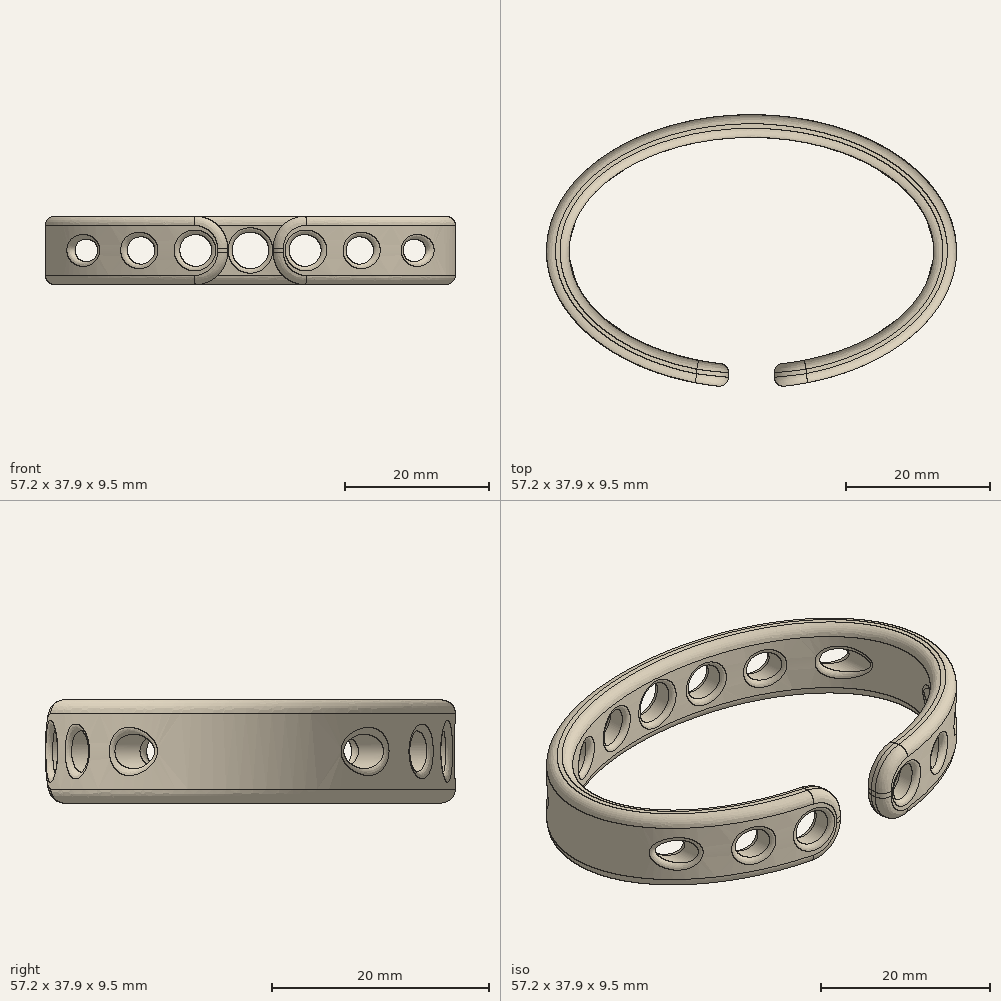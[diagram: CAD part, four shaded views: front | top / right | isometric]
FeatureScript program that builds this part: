
annotation { "Feature Type Name" : "Feature", "Feature Type Description" : "" }
export const myFeature = defineFeature(function(context is Context, id is Id, definition is map)
    precondition{}
    {
        {
            var Q0;
            Q0=qCreatedBy(makeId("Top.planeOp"),FACE);
            var sketch = newSketch(context, id + "F0", { "sketchPlane" : qUnion([Q0])});
            skEllipticalArc(sketch, "E0", {});
            skEllipticalArc(sketch, "E1", {});
            skLineSegment(sketch, "E2.left", {"start": v(-3.18, -17.54) * mm, "end": v(-3.18, -16.9) * mm});
            skLineSegment(sketch, "E2.right", {"start": v(3.17, -17.54) * mm, "end": v(3.17, -16.9) * mm});
            skPoint(sketch, "E3.end.orphan", {"position": v(0, -19.05) * mm});
            skPoint(sketch, "E4.visualSharp", {"position": v(-3.18, -18.93) * mm});
            skArc(sketch, "E4.filletArc", {"start": v(-4.58, -18.8) * mm, "mid": v(-3.6, -18.49) * mm, "end": v(-3.18, -17.54) * mm});
            skPoint(sketch, "E5.visualSharp", {"position": v(3.18, -18.93) * mm});
            skArc(sketch, "E5.filletArc", {"start": v(3.17, -17.54) * mm, "mid": v(3.6, -18.49) * mm, "end": v(4.58, -18.8) * mm});
            skPoint(sketch, "E6.visualSharp", {"position": v(3.17, -15.75) * mm});
            skArc(sketch, "E6.filletArc", {"start": v(4.3, -15.64) * mm, "mid": v(3.5, -16.06) * mm, "end": v(3.17, -16.9) * mm});
            skPoint(sketch, "E7.visualSharp", {"position": v(-3.18, -15.75) * mm});
            skArc(sketch, "E7.filletArc", {"start": v(-3.18, -16.9) * mm, "mid": v(-3.5, -16.06) * mm, "end": v(-4.3, -15.64) * mm});
            const initialGuessF0  = {"E0": [0, 0, 1, 0, 0.0254, 0.015875, 4.8828647943944, 4.541913166455214], "E1": [0, 0, 1, 0, 0.028575, 0.01905, 4.873424775599793, 4.551353185169586]};
            skSetInitialGuess(sketch, initialGuessF0);
            skSolve(sketch);
        }
        {
            var Q0;
            Q0=makeQuery(id+"F0.imprint","IMPRINT",FACE,{"disambiguationData":[TD([[makeQuery(id+"F0.imprint","IMPRINT",EDGE,{"derivedFrom":sQuery(id+"F0.wireOp",EDGE,"E0")}),-1.0]])]});
            extrude(context, id + "F1", {"entities" : qUnion([Q0]), "depth" : 9.52 * mm});
        }
        {
            var Q0;
            Q0=makeQuery(id+"F1.opExtrude","CAP_EDGE",EDGE,{"disambiguationData":[OSD([sQuery(id+"F0.wireOp",EDGE,"E2.left")])],"isStart":false});
            var Q1;
            Q1=makeQuery(id+"F1.opExtrude","CAP_EDGE",EDGE,{"disambiguationData":[OSD([sQuery(id+"F0.wireOp",EDGE,"E2.left")])],"isStart":true});
            var Q2;
            Q2=makeQuery(id+"F1.opExtrude","CAP_EDGE",EDGE,{"disambiguationData":[OSD([sQuery(id+"F0.wireOp",EDGE,"E2.right")])],"isStart":false});
            var Q3;
            Q3=makeQuery(id+"F1.opExtrude","CAP_EDGE",EDGE,{"disambiguationData":[OSD([sQuery(id+"F0.wireOp",EDGE,"E2.right")])],"isStart":true});
            fillet(context, id + "F2", {"entities" : qUnion([Q0, Q1, Q2, Q3]), "radius" : 4.44 * mm, "allowEdgeOverflow" : false});
        }
        {
            var Q0;
            Q0=makeQuery(id+"F1.opExtrude","CAP_EDGE",EDGE,{"disambiguationData":[OSD([sQuery(id+"F0.wireOp",EDGE,"E1")])],"isStart":false});
            var Q1;
            Q1=makeQuery(id+"F1.opExtrude","CAP_EDGE",EDGE,{"disambiguationData":[OSD([sQuery(id+"F0.wireOp",EDGE,"E0")])],"isStart":false});
            var Q2;
            Q2=makeQuery(id+"F1.opExtrude","CAP_EDGE",EDGE,{"disambiguationData":[OSD([sQuery(id+"F0.wireOp",EDGE,"E1")])],"isStart":true});
            var Q3;
            Q3=makeQuery(id+"F1.opExtrude","CAP_EDGE",EDGE,{"disambiguationData":[OSD([sQuery(id+"F0.wireOp",EDGE,"E0")])],"isStart":true});
            fillet(context, id + "F3", {"entities" : qUnion([Q0, Q1, Q2, Q3]), "radius" : 1.27 * mm, "tangentPropagation" : true, "allowEdgeOverflow" : false});
        }
        {
            var Q0;
            Q0=qCreatedBy(makeId("Front.planeOp"),FACE);
            var sketch = newSketch(context, id + "F4", { "sketchPlane" : qUnion([Q0])});
            skCircle(sketch, "E8", {"center": v(-7.62, 4.76) * mm, "radius": 2.22 * mm});
            skCircle(sketch, "E9", {"center": v(0, 4.76) * mm, "radius": 2.54 * mm});
            skCircle(sketch, "E10", {"center": v(7.62, 4.76) * mm, "radius": 2.22 * mm});
            skCircle(sketch, "E11", {"center": v(-15.24, 4.76) * mm, "radius": 1.9 * mm});
            skCircle(sketch, "E12", {"center": v(15.24, 4.76) * mm, "radius": 1.9 * mm});
            skCircle(sketch, "E13", {"center": v(-22.86, 4.76) * mm, "radius": 1.59 * mm});
            skCircle(sketch, "E14", {"center": v(22.86, 4.76) * mm, "radius": 1.59 * mm});
            skSolve(sketch);
        }
        {
            var Q0;
            Q0=makeQuery(id+"F4.imprint","IMPRINT",FACE,{"disambiguationData":[TD([[makeQuery(id+"F4.imprint","IMPRINT",EDGE,{"derivedFrom":sQuery(id+"F4.wireOp",EDGE,"E13")}),1.0]])]});
            var Q1;
            Q1=makeQuery(id+"F4.imprint","IMPRINT",FACE,{"disambiguationData":[TD([[makeQuery(id+"F4.imprint","IMPRINT",EDGE,{"derivedFrom":sQuery(id+"F4.wireOp",EDGE,"E11")}),1.0]])]});
            var Q2;
            Q2=makeQuery(id+"F4.imprint","IMPRINT",FACE,{"disambiguationData":[TD([[makeQuery(id+"F4.imprint","IMPRINT",EDGE,{"derivedFrom":sQuery(id+"F4.wireOp",EDGE,"E8")}),1.0]])]});
            var Q3;
            Q3=makeQuery(id+"F4.imprint","IMPRINT",FACE,{"disambiguationData":[TD([[makeQuery(id+"F4.imprint","IMPRINT",EDGE,{"derivedFrom":sQuery(id+"F4.wireOp",EDGE,"E9")}),1.0]])]});
            var Q4;
            Q4=makeQuery(id+"F4.imprint","IMPRINT",FACE,{"disambiguationData":[TD([[makeQuery(id+"F4.imprint","IMPRINT",EDGE,{"derivedFrom":sQuery(id+"F4.wireOp",EDGE,"E10")}),1.0]])]});
            var Q5;
            Q5=makeQuery(id+"F4.imprint","IMPRINT",FACE,{"disambiguationData":[TD([[makeQuery(id+"F4.imprint","IMPRINT",EDGE,{"derivedFrom":sQuery(id+"F4.wireOp",EDGE,"E12")}),1.0]])]});
            var Q6;
            Q6=makeQuery(id+"F4.imprint","IMPRINT",FACE,{"disambiguationData":[TD([[makeQuery(id+"F4.imprint","IMPRINT",EDGE,{"derivedFrom":sQuery(id+"F4.wireOp",EDGE,"E14")}),1.0]])]});
            extrude(context, id + "F5", {"entities" : qUnion([Q0, Q1, Q2, Q3, Q4, Q5, Q6]), "operationType" : NewBodyOperationType.REMOVE, "endBound" : BoundingType.SYMMETRIC, "depth" : 50.8 * mm});
        }
        {
            var Q0;
            Q0=makeQuery(id+"F5.boolean.opBoolean","INTERSECT",EDGE,{"disambiguationData":[OD(1.0)],"derivedFrom":[makeQuery(id+"F1.opExtrude","SWEPT_FACE",FACE,{"disambiguationData":[OSD([sQuery(id+"F0.wireOp",EDGE,"E0")])]}),makeQuery(id+"F5.opExtrude","SWEPT_FACE",FACE,{"disambiguationData":[OSD([sQuery(id+"F4.wireOp",EDGE,"E13")])]})]});
            var Q1;
            Q1=makeQuery(id+"F5.boolean.opBoolean","INTERSECT",EDGE,{"disambiguationData":[OD(1.0)],"derivedFrom":[makeQuery(id+"F1.opExtrude","SWEPT_FACE",FACE,{"disambiguationData":[OSD([sQuery(id+"F0.wireOp",EDGE,"E0")])]}),makeQuery(id+"F5.opExtrude","SWEPT_FACE",FACE,{"disambiguationData":[OSD([sQuery(id+"F4.wireOp",EDGE,"E11")])]})]});
            var Q2;
            Q2=makeQuery(id+"F5.boolean.opBoolean","INTERSECT",EDGE,{"disambiguationData":[OD(1.0)],"derivedFrom":[makeQuery(id+"F1.opExtrude","SWEPT_FACE",FACE,{"disambiguationData":[OSD([sQuery(id+"F0.wireOp",EDGE,"E0")])]}),makeQuery(id+"F5.opExtrude","SWEPT_FACE",FACE,{"disambiguationData":[OSD([sQuery(id+"F4.wireOp",EDGE,"E8")])]})]});
            var Q3;
            Q3=makeQuery(id+"F5.boolean.opBoolean","INTERSECT",EDGE,{"derivedFrom":[makeQuery(id+"F1.opExtrude","SWEPT_FACE",FACE,{"disambiguationData":[OSD([sQuery(id+"F0.wireOp",EDGE,"E0")])]}),makeQuery(id+"F5.opExtrude","SWEPT_FACE",FACE,{"disambiguationData":[OSD([sQuery(id+"F4.wireOp",EDGE,"E9")])]})]});
            var Q4;
            Q4=makeQuery(id+"F5.boolean.opBoolean","INTERSECT",EDGE,{"disambiguationData":[OD(1.0)],"derivedFrom":[makeQuery(id+"F1.opExtrude","SWEPT_FACE",FACE,{"disambiguationData":[OSD([sQuery(id+"F0.wireOp",EDGE,"E0")])]}),makeQuery(id+"F5.opExtrude","SWEPT_FACE",FACE,{"disambiguationData":[OSD([sQuery(id+"F4.wireOp",EDGE,"E10")])]})]});
            var Q5;
            Q5=makeQuery(id+"F5.boolean.opBoolean","INTERSECT",EDGE,{"disambiguationData":[OD(1.0)],"derivedFrom":[makeQuery(id+"F1.opExtrude","SWEPT_FACE",FACE,{"disambiguationData":[OSD([sQuery(id+"F0.wireOp",EDGE,"E0")])]}),makeQuery(id+"F5.opExtrude","SWEPT_FACE",FACE,{"disambiguationData":[OSD([sQuery(id+"F4.wireOp",EDGE,"E12")])]})]});
            var Q6;
            Q6=makeQuery(id+"F5.boolean.opBoolean","INTERSECT",EDGE,{"disambiguationData":[OD(1.0)],"derivedFrom":[makeQuery(id+"F1.opExtrude","SWEPT_FACE",FACE,{"disambiguationData":[OSD([sQuery(id+"F0.wireOp",EDGE,"E0")])]}),makeQuery(id+"F5.opExtrude","SWEPT_FACE",FACE,{"disambiguationData":[OSD([sQuery(id+"F4.wireOp",EDGE,"E14")])]})]});
            var Q7;
            Q7=makeQuery(id+"F5.boolean.opBoolean","INTERSECT",EDGE,{"disambiguationData":[OD(1.0)],"derivedFrom":[makeQuery(id+"F1.opExtrude","SWEPT_FACE",FACE,{"disambiguationData":[OSD([sQuery(id+"F0.wireOp",EDGE,"E1")])]}),makeQuery(id+"F5.opExtrude","SWEPT_FACE",FACE,{"disambiguationData":[OSD([sQuery(id+"F4.wireOp",EDGE,"E14")])]})]});
            var Q8;
            Q8=makeQuery(id+"F5.boolean.opBoolean","INTERSECT",EDGE,{"disambiguationData":[OD(1.0)],"derivedFrom":[makeQuery(id+"F1.opExtrude","SWEPT_FACE",FACE,{"disambiguationData":[OSD([sQuery(id+"F0.wireOp",EDGE,"E1")])]}),makeQuery(id+"F5.opExtrude","SWEPT_FACE",FACE,{"disambiguationData":[OSD([sQuery(id+"F4.wireOp",EDGE,"E12")])]})]});
            var Q9;
            Q9=makeQuery(id+"F5.boolean.opBoolean","INTERSECT",EDGE,{"disambiguationData":[OD(1.0)],"derivedFrom":[makeQuery(id+"F1.opExtrude","SWEPT_FACE",FACE,{"disambiguationData":[OSD([sQuery(id+"F0.wireOp",EDGE,"E1")])]}),makeQuery(id+"F5.opExtrude","SWEPT_FACE",FACE,{"disambiguationData":[OSD([sQuery(id+"F4.wireOp",EDGE,"E10")])]})]});
            var Q10;
            Q10=makeQuery(id+"F5.boolean.opBoolean","INTERSECT",EDGE,{"derivedFrom":[makeQuery(id+"F1.opExtrude","SWEPT_FACE",FACE,{"disambiguationData":[OSD([sQuery(id+"F0.wireOp",EDGE,"E1")])]}),makeQuery(id+"F5.opExtrude","SWEPT_FACE",FACE,{"disambiguationData":[OSD([sQuery(id+"F4.wireOp",EDGE,"E9")])]})]});
            var Q11;
            Q11=makeQuery(id+"F5.boolean.opBoolean","INTERSECT",EDGE,{"disambiguationData":[OD(1.0)],"derivedFrom":[makeQuery(id+"F1.opExtrude","SWEPT_FACE",FACE,{"disambiguationData":[OSD([sQuery(id+"F0.wireOp",EDGE,"E1")])]}),makeQuery(id+"F5.opExtrude","SWEPT_FACE",FACE,{"disambiguationData":[OSD([sQuery(id+"F4.wireOp",EDGE,"E8")])]})]});
            var Q12;
            Q12=makeQuery(id+"F5.boolean.opBoolean","INTERSECT",EDGE,{"disambiguationData":[OD(1.0)],"derivedFrom":[makeQuery(id+"F1.opExtrude","SWEPT_FACE",FACE,{"disambiguationData":[OSD([sQuery(id+"F0.wireOp",EDGE,"E1")])]}),makeQuery(id+"F5.opExtrude","SWEPT_FACE",FACE,{"disambiguationData":[OSD([sQuery(id+"F4.wireOp",EDGE,"E11")])]})]});
            var Q13;
            Q13=makeQuery(id+"F5.boolean.opBoolean","INTERSECT",EDGE,{"disambiguationData":[OD(1.0)],"derivedFrom":[makeQuery(id+"F1.opExtrude","SWEPT_FACE",FACE,{"disambiguationData":[OSD([sQuery(id+"F0.wireOp",EDGE,"E1")])]}),makeQuery(id+"F5.opExtrude","SWEPT_FACE",FACE,{"disambiguationData":[OSD([sQuery(id+"F4.wireOp",EDGE,"E13")])]})]});
            var Q14;
            Q14=makeQuery(id+"F5.boolean.opBoolean","INTERSECT",EDGE,{"disambiguationData":[OD(0.0)],"derivedFrom":[makeQuery(id+"F1.opExtrude","SWEPT_FACE",FACE,{"disambiguationData":[OSD([sQuery(id+"F0.wireOp",EDGE,"E0")])]}),makeQuery(id+"F5.opExtrude","SWEPT_FACE",FACE,{"disambiguationData":[OSD([sQuery(id+"F4.wireOp",EDGE,"E8")])]})]});
            var Q15;
            Q15=makeQuery(id+"F5.boolean.opBoolean","INTERSECT",EDGE,{"disambiguationData":[OD(0.0)],"derivedFrom":[makeQuery(id+"F1.opExtrude","SWEPT_FACE",FACE,{"disambiguationData":[OSD([sQuery(id+"F0.wireOp",EDGE,"E1")])]}),makeQuery(id+"F5.opExtrude","SWEPT_FACE",FACE,{"disambiguationData":[OSD([sQuery(id+"F4.wireOp",EDGE,"E8")])]})]});
            var Q16;
            Q16=makeQuery(id+"F5.boolean.opBoolean","INTERSECT",EDGE,{"disambiguationData":[OD(0.0)],"derivedFrom":[makeQuery(id+"F1.opExtrude","SWEPT_FACE",FACE,{"disambiguationData":[OSD([sQuery(id+"F0.wireOp",EDGE,"E1")])]}),makeQuery(id+"F5.opExtrude","SWEPT_FACE",FACE,{"disambiguationData":[OSD([sQuery(id+"F4.wireOp",EDGE,"E11")])]})]});
            var Q17;
            Q17=makeQuery(id+"F5.boolean.opBoolean","INTERSECT",EDGE,{"disambiguationData":[OD(0.0)],"derivedFrom":[makeQuery(id+"F1.opExtrude","SWEPT_FACE",FACE,{"disambiguationData":[OSD([sQuery(id+"F0.wireOp",EDGE,"E0")])]}),makeQuery(id+"F5.opExtrude","SWEPT_FACE",FACE,{"disambiguationData":[OSD([sQuery(id+"F4.wireOp",EDGE,"E11")])]})]});
            var Q18;
            Q18=makeQuery(id+"F5.boolean.opBoolean","INTERSECT",EDGE,{"disambiguationData":[OD(0.0)],"derivedFrom":[makeQuery(id+"F1.opExtrude","SWEPT_FACE",FACE,{"disambiguationData":[OSD([sQuery(id+"F0.wireOp",EDGE,"E1")])]}),makeQuery(id+"F5.opExtrude","SWEPT_FACE",FACE,{"disambiguationData":[OSD([sQuery(id+"F4.wireOp",EDGE,"E13")])]})]});
            var Q19;
            Q19=makeQuery(id+"F5.boolean.opBoolean","INTERSECT",EDGE,{"disambiguationData":[OD(0.0)],"derivedFrom":[makeQuery(id+"F1.opExtrude","SWEPT_FACE",FACE,{"disambiguationData":[OSD([sQuery(id+"F0.wireOp",EDGE,"E0")])]}),makeQuery(id+"F5.opExtrude","SWEPT_FACE",FACE,{"disambiguationData":[OSD([sQuery(id+"F4.wireOp",EDGE,"E13")])]})]});
            var Q20;
            Q20=makeQuery(id+"F5.boolean.opBoolean","INTERSECT",EDGE,{"disambiguationData":[OD(0.0)],"derivedFrom":[makeQuery(id+"F1.opExtrude","SWEPT_FACE",FACE,{"disambiguationData":[OSD([sQuery(id+"F0.wireOp",EDGE,"E0")])]}),makeQuery(id+"F5.opExtrude","SWEPT_FACE",FACE,{"disambiguationData":[OSD([sQuery(id+"F4.wireOp",EDGE,"E10")])]})]});
            var Q21;
            Q21=makeQuery(id+"F5.boolean.opBoolean","INTERSECT",EDGE,{"disambiguationData":[OD(0.0)],"derivedFrom":[makeQuery(id+"F1.opExtrude","SWEPT_FACE",FACE,{"disambiguationData":[OSD([sQuery(id+"F0.wireOp",EDGE,"E0")])]}),makeQuery(id+"F5.opExtrude","SWEPT_FACE",FACE,{"disambiguationData":[OSD([sQuery(id+"F4.wireOp",EDGE,"E12")])]})]});
            var Q22;
            Q22=makeQuery(id+"F5.boolean.opBoolean","INTERSECT",EDGE,{"disambiguationData":[OD(0.0)],"derivedFrom":[makeQuery(id+"F1.opExtrude","SWEPT_FACE",FACE,{"disambiguationData":[OSD([sQuery(id+"F0.wireOp",EDGE,"E0")])]}),makeQuery(id+"F5.opExtrude","SWEPT_FACE",FACE,{"disambiguationData":[OSD([sQuery(id+"F4.wireOp",EDGE,"E14")])]})]});
            var Q23;
            Q23=makeQuery(id+"F5.boolean.opBoolean","INTERSECT",EDGE,{"disambiguationData":[OD(0.0)],"derivedFrom":[makeQuery(id+"F1.opExtrude","SWEPT_FACE",FACE,{"disambiguationData":[OSD([sQuery(id+"F0.wireOp",EDGE,"E1")])]}),makeQuery(id+"F5.opExtrude","SWEPT_FACE",FACE,{"disambiguationData":[OSD([sQuery(id+"F4.wireOp",EDGE,"E10")])]})]});
            var Q24;
            Q24=makeQuery(id+"F5.boolean.opBoolean","INTERSECT",EDGE,{"disambiguationData":[OD(0.0)],"derivedFrom":[makeQuery(id+"F1.opExtrude","SWEPT_FACE",FACE,{"disambiguationData":[OSD([sQuery(id+"F0.wireOp",EDGE,"E1")])]}),makeQuery(id+"F5.opExtrude","SWEPT_FACE",FACE,{"disambiguationData":[OSD([sQuery(id+"F4.wireOp",EDGE,"E12")])]})]});
            var Q25;
            Q25=makeQuery(id+"F5.boolean.opBoolean","INTERSECT",EDGE,{"disambiguationData":[OD(0.0)],"derivedFrom":[makeQuery(id+"F1.opExtrude","SWEPT_FACE",FACE,{"disambiguationData":[OSD([sQuery(id+"F0.wireOp",EDGE,"E1")])]}),makeQuery(id+"F5.opExtrude","SWEPT_FACE",FACE,{"disambiguationData":[OSD([sQuery(id+"F4.wireOp",EDGE,"E14")])]})]});
            fillet(context, id + "F6", {"entities" : qUnion([Q0, Q1, Q2, Q3, Q4, Q5, Q6, Q7, Q8, Q9, Q10, Q11, Q12, Q13, Q14, Q15, Q16, Q17, Q18, Q19, Q20, Q21, Q22, Q23, Q24, Q25]), "radius" : 0.64 * mm, "tangentPropagation" : true, "allowEdgeOverflow" : false});
        }
    });
